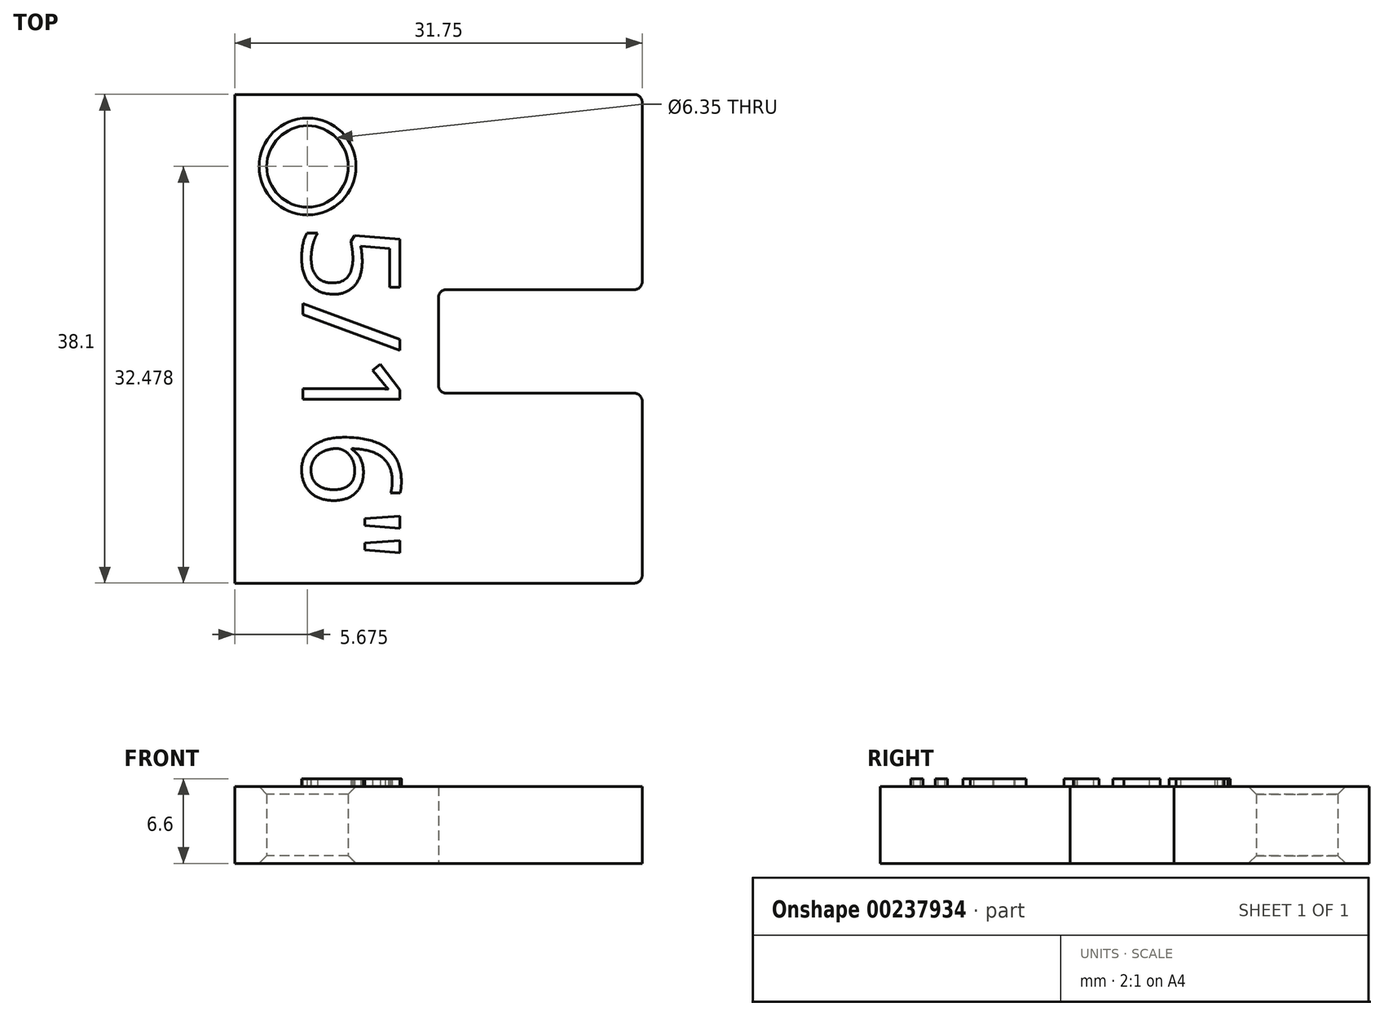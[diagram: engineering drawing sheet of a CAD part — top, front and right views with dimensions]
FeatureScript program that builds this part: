
annotation { "Feature Type Name" : "Feature", "Feature Type Description" : "" }
export const myFeature = defineFeature(function(context is Context, id is Id, definition is map)
    precondition{}
    {
        {
            var Q0;
            Q0=qCreatedBy(makeId("Top.planeOp"),FACE);
            var sketch = newSketch(context, id + "F0", { "sketchPlane" : qUnion([Q0])});
            skLineSegment(sketch, "E0", {"start": v(-21.73, 28.53) * mm, "end": v(10.02, 28.53) * mm});
            skLineSegment(sketch, "E1", {"start": v(10.02, 28.53) * mm, "end": v(10.02, 13.3) * mm});
            skLineSegment(sketch, "E2", {"start": v(10.02, 13.3) * mm, "end": v(-5.86, 13.3) * mm});
            skLineSegment(sketch, "E3", {"start": v(-5.86, 13.3) * mm, "end": v(-5.86, 5.23) * mm});
            skLineSegment(sketch, "E4", {"start": v(-5.86, 5.23) * mm, "end": v(10.02, 5.23) * mm});
            skLineSegment(sketch, "E5", {"start": v(10.02, 5.23) * mm, "end": v(10.02, -9.57) * mm});
            skLineSegment(sketch, "E6", {"start": v(10.02, -9.57) * mm, "end": v(-21.73, -9.57) * mm});
            skLineSegment(sketch, "E7", {"start": v(-21.73, 28.53) * mm, "end": v(-21.73, -9.57) * mm});
            skCircle(sketch, "E8", {"center": v(-16.06, 22.9) * mm, "radius": 3.18 * mm});
            skSolve(sketch);
        }
        {
            var Q0;
            Q0 = qSketchRegion(id + "F0", true);
            extrude(context, id + "F1", {"entities" : qUnion([Q0]), "depth" : 6 * mm});
        }
        {
            var Q0;
            Q0=makeQuery(id+"F1.opExtrude","SWEPT_EDGE",EDGE,{"disambiguationData":[OSD([sQuery(id+"F0.wireOp",EDGE,"E5"),sQuery(id+"F0.wireOp",EDGE,"E6")])]});
            var Q1;
            Q1=makeQuery(id+"F1.opExtrude","SWEPT_EDGE",EDGE,{"disambiguationData":[OSD([sQuery(id+"F0.wireOp",EDGE,"E4"),sQuery(id+"F0.wireOp",EDGE,"E5")])]});
            var Q2;
            Q2=makeQuery(id+"F1.opExtrude","SWEPT_EDGE",EDGE,{"disambiguationData":[OSD([sQuery(id+"F0.wireOp",EDGE,"E1"),sQuery(id+"F0.wireOp",EDGE,"E2")])]});
            var Q3;
            Q3=makeQuery(id+"F1.opExtrude","SWEPT_EDGE",EDGE,{"disambiguationData":[OSD([sQuery(id+"F0.wireOp",EDGE,"E2"),sQuery(id+"F0.wireOp",EDGE,"E3")])]});
            var Q4;
            Q4=makeQuery(id+"F1.opExtrude","SWEPT_EDGE",EDGE,{"disambiguationData":[OSD([sQuery(id+"F0.wireOp",EDGE,"E3"),sQuery(id+"F0.wireOp",EDGE,"E4")])]});
            var Q5;
            Q5=makeQuery(id+"F1.opExtrude","SWEPT_EDGE",EDGE,{"disambiguationData":[OSD([sQuery(id+"F0.wireOp",EDGE,"E0"),sQuery(id+"F0.wireOp",EDGE,"E1")])]});
            fillet(context, id + "F2", {"entities" : qUnion([Q0, Q1, Q2, Q3, Q4, Q5]), "radius" : .6 * mm, "tangentPropagation" : true, "allowEdgeOverflow" : false});
        }
        {
            var Q0;
            Q0=makeQuery(id+"F1.opExtrude","CAP_EDGE",EDGE,{"disambiguationData":[OSD([sQuery(id+"F0.wireOp",EDGE,"E8")])],"isStart":false});
            var Q1;
            Q1=makeQuery(id+"F1.opExtrude","CAP_EDGE",EDGE,{"disambiguationData":[OSD([sQuery(id+"F0.wireOp",EDGE,"E8")])],"isStart":true});
            chamfer(context, id + "F3", {"entities" : qUnion([Q0, Q1]), "width" : .6 * mm, "tangentPropagation" : true});
        }
        {
            var Q0;
            Q0=makeQuery(id+"F1.opExtrude","CAP_FACE",FACE,{"disambiguationData":[OSD([sQuery(id+"F0.wireOp",EDGE,"E0"),sQuery(id+"F0.wireOp",EDGE,"E1"),sQuery(id+"F0.wireOp",EDGE,"E2"),sQuery(id+"F0.wireOp",EDGE,"E3"),sQuery(id+"F0.wireOp",EDGE,"E4"),sQuery(id+"F0.wireOp",EDGE,"E5"),sQuery(id+"F0.wireOp",EDGE,"E6"),sQuery(id+"F0.wireOp",EDGE,"E7"),sQuery(id+"F0.wireOp",EDGE,"E8")])],"isStart":false});
            var sketch = newSketch(context, id + "F4", { "sketchPlane" : qUnion([Q0])});
            skText(sketch, "E9", { "text": "5/16\"", "fontName": "OpenSans-Regular.ttf"});
            const initialGuessF4  = {"E9": [-0.01641, 0.01839, 0, -1, 0.00762]};
            skSetInitialGuess(sketch, initialGuessF4);
            skSolve(sketch);
        }
        {
            var Q0;
            Q0 = qSketchRegion(id + "F4", true);
            var Q1;
            Q1=makeQuery(id+"F1.opExtrude","CAP_FACE",FACE,{"disambiguationData":[OSD([sQuery(id+"F0.wireOp",EDGE,"E0"),sQuery(id+"F0.wireOp",EDGE,"E1"),sQuery(id+"F0.wireOp",EDGE,"E2"),sQuery(id+"F0.wireOp",EDGE,"E3"),sQuery(id+"F0.wireOp",EDGE,"E4"),sQuery(id+"F0.wireOp",EDGE,"E5"),sQuery(id+"F0.wireOp",EDGE,"E6"),sQuery(id+"F0.wireOp",EDGE,"E7"),sQuery(id+"F0.wireOp",EDGE,"E8")])],"isStart":true});
            extrude(context, id + "F5", {"entities" : qUnion([Q0]), "operationType" : NewBodyOperationType.ADD, "endBoundEntityFace" : qUnion([Q1]), "depth" : .6 * mm});
        }
    });
